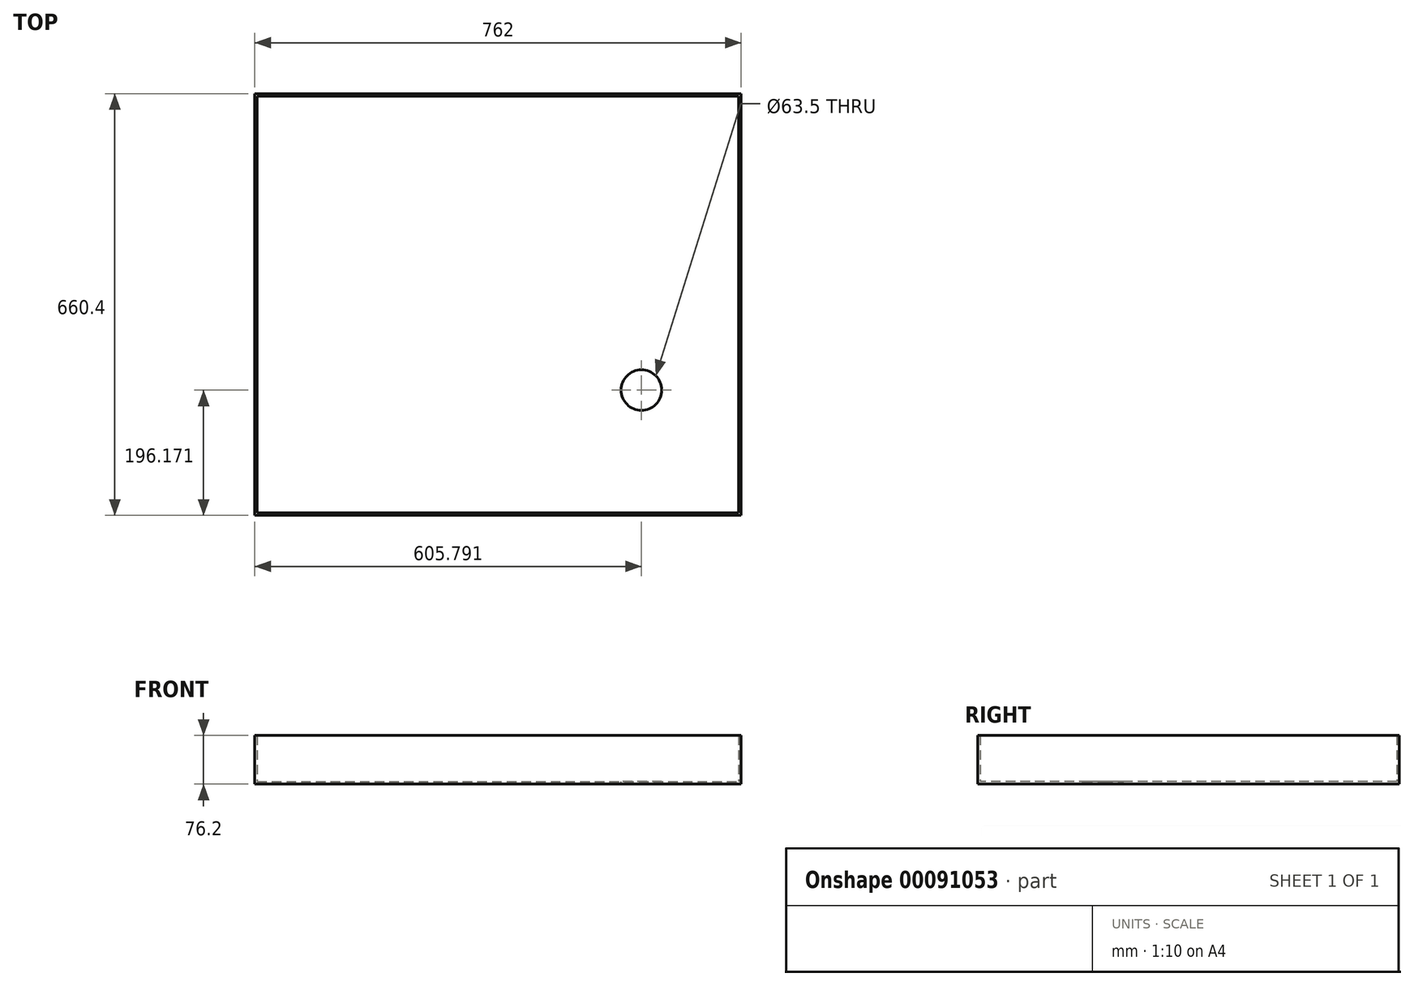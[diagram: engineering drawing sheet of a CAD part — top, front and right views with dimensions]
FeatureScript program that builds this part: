
annotation { "Feature Type Name" : "Feature", "Feature Type Description" : "" }
export const myFeature = defineFeature(function(context is Context, id is Id, definition is map)
    precondition{}
    {
        {
            var Q0;
            Q0=qCreatedBy(makeId("Top.planeOp"),FACE);
            var sketch = newSketch(context, id + "F0", { "sketchPlane" : qUnion([Q0])});
            skLineSegment(sketch, "E0.bottom", {"start": v(-452.17, 399.2) * mm, "end": v(309.83, 399.2) * mm});
            skLineSegment(sketch, "E0.top", {"start": v(-452.17, -261.2) * mm, "end": v(309.83, -261.2) * mm});
            skLineSegment(sketch, "E0.left", {"start": v(-452.17, 399.2) * mm, "end": v(-452.17, -261.2) * mm});
            skLineSegment(sketch, "E0.right", {"start": v(309.83, 399.2) * mm, "end": v(309.83, -261.2) * mm});
            skSolve(sketch);
        }
        {
            var Q0;
            Q0 = qSketchRegion(id + "F0", true);
            extrude(context, id + "F1", {"entities" : qUnion([Q0]), "depth" : 76.2 * mm});
        }
        {
            var Q0;
            Q0=makeQuery(id+"F1.opExtrude","CAP_FACE",FACE,{"disambiguationData":[OSD([sQuery(id+"F0.wireOp",EDGE,"E0.bottom"),sQuery(id+"F0.wireOp",EDGE,"E0.top"),sQuery(id+"F0.wireOp",EDGE,"E0.left"),sQuery(id+"F0.wireOp",EDGE,"E0.right")])],"isStart":false});
            shell(context, id + "F2", {"entities" : qUnion([Q0]), "thickness" : 3.8 * mm});
        }
        {
            var Q0;
            Q0=makeQuery(id+"F2.opShell","OFFSET_FACE",FACE,{"disambiguationData":[OSD([sQuery(id+"F0.wireOp",EDGE,"E0.bottom"),sQuery(id+"F0.wireOp",EDGE,"E0.top"),sQuery(id+"F0.wireOp",EDGE,"E0.left"),sQuery(id+"F0.wireOp",EDGE,"E0.right")])]});
            var sketch = newSketch(context, id + "F3", { "sketchPlane" : qUnion([Q0])});
            skCircle(sketch, "E1", {"center": v(153.62, -65.03) * mm, "radius": 31.75 * mm});
            skSolve(sketch);
        }
        {
            var Q0;
            Q0 = qSketchRegion(id + "F3", true);
            extrude(context, id + "F4", {"entities" : qUnion([Q0]), "operationType" : NewBodyOperationType.REMOVE, "endBound" : BoundingType.THROUGH_ALL, "oppositeDirection" : true, "depth" : 25.4 * mm});
        }
    });
